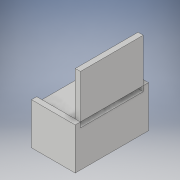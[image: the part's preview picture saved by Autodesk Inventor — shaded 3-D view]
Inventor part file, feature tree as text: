
AUTODESK INVENTOR PART (.ipt)
format: ipt  version: 2019 (Build 230136000, 136)  size: 119,808 bytes
history: native  units: mm
features: extrude x3, sketch x3
ambient origin geometry x8: Origin, YZ Plane, XZ Plane, XY Plane, X Axis, Y Axis, Z Axis, Center Point
bodies: Solid1 (feature_tree)
feature tree (6):
  extrude  "Extrusion1"  Depth=830.0mm
  extrude  "Extrusion2"  Depth=59.0mm
  extrude  "Extrusion3"  Depth=58.5mm TaperAngle=0.0deg
  sketch  "Sketch1"  dims[d0=495.0mm d1=830.0mm]
  sketch  "Sketch2"  dims[d2=472.0mm d3=0.0mm d4=59.0mm]
  sketch  "Sketch3"  dims[d5=59.0mm d6=58.5mm d7=0.0mm d8=495.0mm d9=58.5mm d10=0.0mm]
